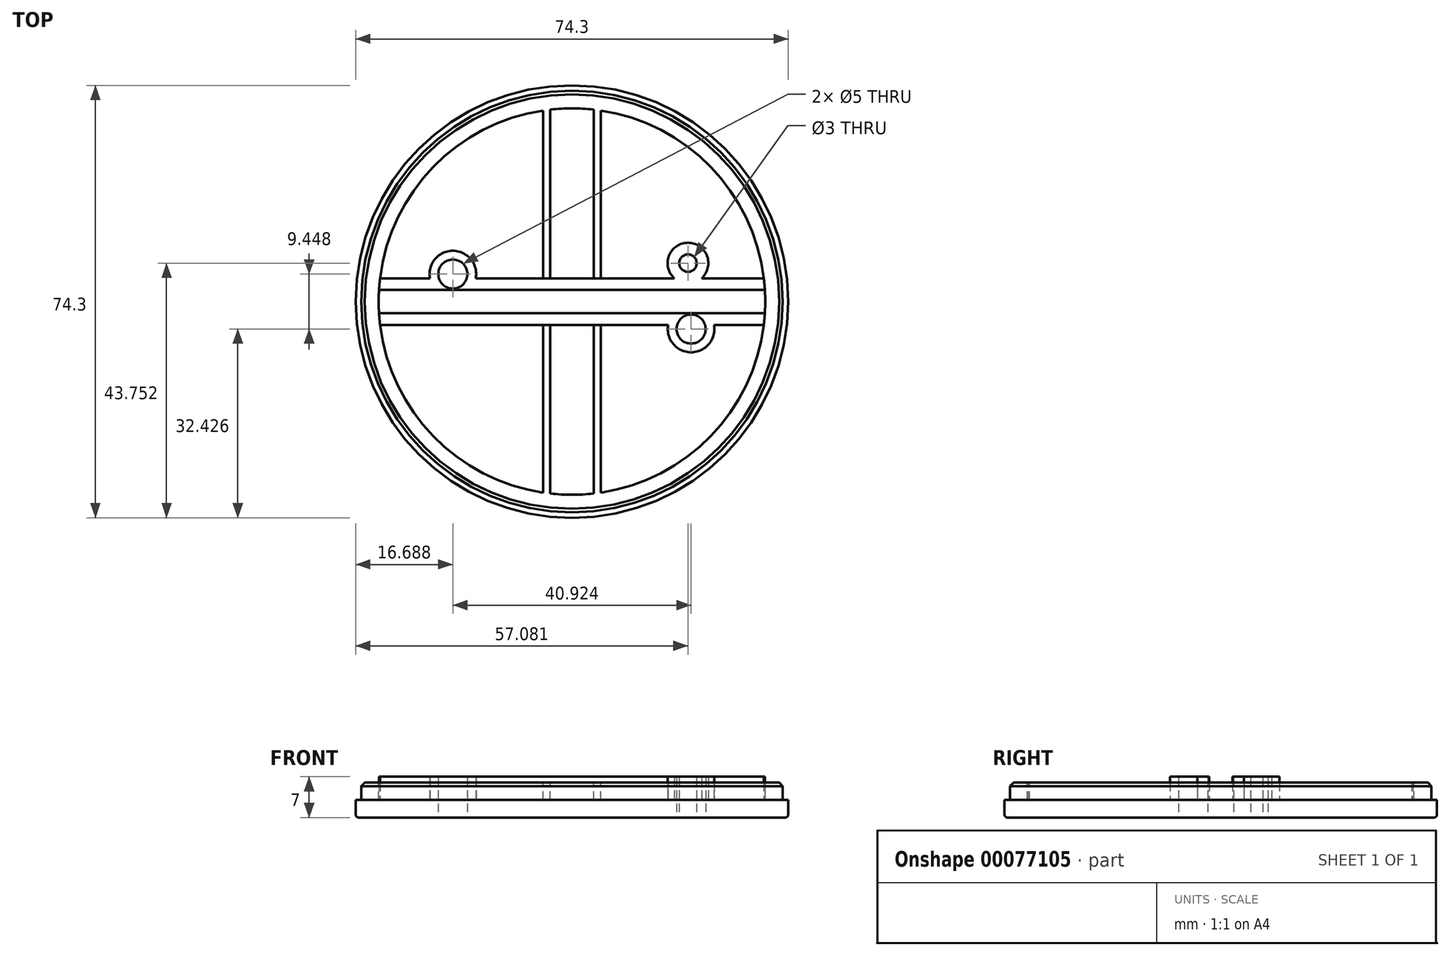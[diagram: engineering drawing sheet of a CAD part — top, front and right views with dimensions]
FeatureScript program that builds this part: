
annotation { "Feature Type Name" : "Feature", "Feature Type Description" : "" }
export const myFeature = defineFeature(function(context is Context, id is Id, definition is map)
    precondition{}
    {
        {
            var Q0;
            Q0=qCreatedBy(makeId("Front.planeOp"),FACE);
            var sketch = newSketch(context, id + "F0", { "sketchPlane" : qUnion([Q0])});
            skLineSegment(sketch, "E0.bottom", {"start": v(0, 0) * mm, "end": v(-33.2, 0) * mm});
            skLineSegment(sketch, "E0.top", {"start": v(0, -3) * mm, "end": v(-37.15, -3) * mm});
            skLineSegment(sketch, "E0.left", {"start": v(0, 0) * mm, "end": v(0, -3) * mm});
            skLineSegment(sketch, "E0.right", {"start": v(-37.15, 0) * mm, "end": v(-37.15, -3) * mm});
            skLineSegment(sketch, "E1.top", {"start": v(-36.2, 3) * mm, "end": v(-33.2, 3) * mm});
            skLineSegment(sketch, "E1.left", {"start": v(-36.2, 0) * mm, "end": v(-36.2, 3) * mm});
            skLineSegment(sketch, "E1.right", {"start": v(-33.2, 0) * mm, "end": v(-33.2, 3) * mm});
            skLineSegment(sketch, "E2.trimOffspring", {"start": v(-36.2, 0) * mm, "end": v(-37.15, 0) * mm});
            skLineSegment(sketch, "E3", {"start": v(0, 23.02) * mm, "end": v(0, -39) * mm, "construction": true});
            skSolve(sketch);
        }
        {
            var Q0;
            Q0=makeQuery(id+"F0.imprint","IMPRINT",FACE,{"disambiguationData":[TD([[makeQuery(id+"F0.imprint","IMPRINT",EDGE,{"derivedFrom":sQuery(id+"F0.wireOp",EDGE,"E0.bottom")}),1.0]])]});
            var Q1;
            Q1=sQuery(id+"F0.wireOp",EDGE,"E3");
            revolve(context, id + "F1", {"surfaceOperationType" : NewSurfaceOperationType.NEW, "entities" : qUnion([Q0]), "axis" : qUnion([Q1]), "revolveType" : RevolveType.FULL});
        }
        {
            var Q0;
            Q0=makeQuery(id+"F1.opRevolve","SWEPT_FACE",FACE,{"disambiguationData":[OSD([sQuery(id+"F0.wireOp",EDGE,"E0.bottom")])]});
            var sketch = newSketch(context, id + "F2", { "sketchPlane" : qUnion([Q0])});
            skLineSegment(sketch, "E4.bottom", {"start": v(-34.3, 2) * mm, "end": v(34, 2) * mm});
            skLineSegment(sketch, "E4.top", {"start": v(-34.3, 4) * mm, "end": v(34, 4) * mm});
            skLineSegment(sketch, "E4.left", {"start": v(-34.3, 2) * mm, "end": v(-34.3, 4) * mm});
            skLineSegment(sketch, "E4.right", {"start": v(34, 2) * mm, "end": v(34, 4) * mm});
            skLineSegment(sketch, "E5.MirrorCS", {"start": v(-34.3, -2) * mm, "end": v(34, -2) * mm});
            skLineSegment(sketch, "E6.MirrorCS", {"start": v(-34.3, -2) * mm, "end": v(-34.3, -4) * mm});
            skLineSegment(sketch, "E7.MirrorCS", {"start": v(-34.3, -4) * mm, "end": v(34, -4) * mm});
            skLineSegment(sketch, "E8.MirrorCS", {"start": v(34, -2) * mm, "end": v(34, -4) * mm});
            skSolve(sketch);
        }
        {
            var Q0;
            {var subQ0=sQuery(id+"F2.wireOp",EDGE,"E4.bottom");var subQ1=makeQuery(id+"F1.opRevolve","SWEPT_EDGE",EDGE,{"disambiguationData":[OSD([sQuery(id+"F0.wireOp",EDGE,"E0.bottom"),sQuery(id+"F0.wireOp",EDGE,"E1.right")])]});var subQ2=makeQuery(id+"F2.imprint","INTERSECT",VERTEX,{"disambiguationData":[OD(0.0)],"derivedFrom":[subQ1,subQ0]});Q0=makeQuery(id+"F2.imprint","IMPRINT",FACE,{"disambiguationData":[TD([[makeQuery(id+"F2.imprint","IMPRINT",EDGE,{"disambiguationData":[TD([[subQ2,-1.0]])],"derivedFrom":subQ0}),1.0]])]});}
            var Q1;
            {var subQ0=sQuery(id+"F2.wireOp",EDGE,"E5.MirrorCS");var subQ1=makeQuery(id+"F1.opRevolve","SWEPT_EDGE",EDGE,{"disambiguationData":[OSD([sQuery(id+"F0.wireOp",EDGE,"E0.bottom"),sQuery(id+"F0.wireOp",EDGE,"E1.right")])]});var subQ2=makeQuery(id+"F2.imprint","INTERSECT",VERTEX,{"disambiguationData":[OD(0.0)],"derivedFrom":[subQ1,subQ0]});Q1=makeQuery(id+"F2.imprint","IMPRINT",FACE,{"disambiguationData":[TD([[makeQuery(id+"F2.imprint","IMPRINT",EDGE,{"disambiguationData":[TD([[subQ2,-1.0]])],"derivedFrom":subQ0}),-1.0]])]});}
            extrude(context, id + "F3", {"entities" : qUnion([Q0, Q1]), "operationType" : NewBodyOperationType.ADD, "depth" : 4 * mm, "offsetDistance" : 25 * mm});
        }
        {
            var Q0;
            Q0=makeQuery(id+"F3.boolean.opBoolean","SPLIT",FACE,{"disambiguationData":[TD([makeQuery(id+"F3.opExtrude","SWEPT_FACE",FACE,{"disambiguationData":[OSD([sQuery(id+"F2.wireOp",EDGE,"E4.top")])]})])],"derivedFrom":makeQuery(id+"F1.opRevolve","SWEPT_FACE",FACE,{"disambiguationData":[OSD([sQuery(id+"F0.wireOp",EDGE,"E0.bottom")])]})});
            var sketch = newSketch(context, id + "F4", { "sketchPlane" : qUnion([Q0])});
            skCircle(sketch, "E9", {"center": v(0, 0) * mm, "radius": 25 * mm});
            skSolve(sketch);
        }
        {
            var Q0;
            {var subQ0=sQuery(id+"F4.wireOp",EDGE,"E9");var subQ1=sQuery(id+"F2.wireOp",EDGE,"E4.top");var subQ2=makeQuery(id+"F3.opExtrude","CAP_EDGE",EDGE,{"disambiguationData":[OSD([subQ1])],"isStart":true});var subQ3=makeQuery(id+"F4.imprint","INTERSECT",VERTEX,{"disambiguationData":[OD(0.0)],"derivedFrom":[subQ2,subQ0]});Q0=makeQuery(id+"F4.imprint","IMPRINT",FACE,{"disambiguationData":[TD([[makeQuery(id+"F4.imprint","IMPRINT",EDGE,{"disambiguationData":[TD([[subQ3,1.0]])],"derivedFrom":subQ0}),-1.0]])]});}
            var sketch = newSketch(context, id + "F5", { "sketchPlane" : qUnion([Q0])});
            skLineSegment(sketch, "E10", {"start": v(-33.33, 7.7) * mm, "end": v(0, 0) * mm, "construction": true});
            skLineSegment(sketch, "E11", {"start": v(0, 0) * mm, "end": v(33.42, -7.72) * mm, "construction": true});
            skLineSegment(sketch, "E12.bottom", {"start": v(-4.93, 3.16) * mm, "end": v(-3.73, 3.16) * mm});
            skLineSegment(sketch, "E12.top", {"start": v(-4.93, 33.8) * mm, "end": v(-3.73, 33.8) * mm});
            skLineSegment(sketch, "E12.left", {"start": v(-4.93, 3.16) * mm, "end": v(-4.93, 33.8) * mm});
            skLineSegment(sketch, "E12.right", {"start": v(-3.73, 3.16) * mm, "end": v(-3.73, 33.8) * mm});
            skLineSegment(sketch, "E13.MirrorCS", {"start": v(3.73, 3.16) * mm, "end": v(3.73, 33.8) * mm});
            skLineSegment(sketch, "E14.MirrorCS", {"start": v(4.93, 3.16) * mm, "end": v(4.93, 33.8) * mm});
            skLineSegment(sketch, "E15.MirrorCS", {"start": v(4.93, 33.8) * mm, "end": v(3.73, 33.8) * mm});
            skLineSegment(sketch, "E16.MirrorCS", {"start": v(4.93, 3.16) * mm, "end": v(3.73, 3.16) * mm});
            skLineSegment(sketch, "E17.MirrorCS", {"start": v(-4.93, -33.8) * mm, "end": v(-3.73, -33.8) * mm});
            skLineSegment(sketch, "E18.MirrorCS", {"start": v(-3.73, -3.16) * mm, "end": v(-3.73, -33.8) * mm});
            skLineSegment(sketch, "E19.MirrorCS", {"start": v(-4.93, -3.16) * mm, "end": v(-3.73, -3.16) * mm});
            skLineSegment(sketch, "E20.MirrorCS", {"start": v(-4.93, -3.16) * mm, "end": v(-4.93, -33.8) * mm});
            skLineSegment(sketch, "E21.MirrorCS", {"start": v(4.93, -3.16) * mm, "end": v(3.73, -3.16) * mm});
            skLineSegment(sketch, "E22.MirrorCS", {"start": v(4.93, -33.8) * mm, "end": v(3.73, -33.8) * mm});
            skLineSegment(sketch, "E23.MirrorCS", {"start": v(3.73, -3.16) * mm, "end": v(3.73, -33.8) * mm});
            skLineSegment(sketch, "E24.MirrorCS", {"start": v(4.93, -3.16) * mm, "end": v(4.93, -33.8) * mm});
            skCircle(sketch, "E25", {"center": v(0, 0) * mm, "radius": 21 * mm, "construction": true});
            skCircle(sketch, "E26", {"center": v(-20.46, 4.72) * mm, "radius": 2.5 * mm});
            skCircle(sketch, "E27", {"center": v(20.46, -4.72) * mm, "radius": 2.5 * mm});
            skArc(sketch, "E28", {"start": v(-17.49, 2.05) * mm, "mid": v(-20.46, 8.72) * mm, "end": v(-23.44, 2.05) * mm});
            skArc(sketch, "E29", {"start": v(17.54, -2) * mm, "mid": v(20.46, -8.72) * mm, "end": v(23.38, -2) * mm});
            skLineSegment(sketch, "E30", {"start": v(-23.44, 2.05) * mm, "end": v(-17.49, 2.05) * mm});
            skLineSegment(sketch, "E31", {"start": v(17.54, -2) * mm, "end": v(23.38, -2) * mm});
            skSolve(sketch);
        }
        {
            var Q0;
            Q0=makeQuery(id+"F5.imprint","IMPRINT",FACE,{"disambiguationData":[TD([[makeQuery(id+"F5.imprint","IMPRINT",EDGE,{"derivedFrom":sQuery(id+"F5.wireOp",EDGE,"E17.MirrorCS")}),1.0]])]});
            var Q1;
            Q1=makeQuery(id+"F5.imprint","IMPRINT",FACE,{"disambiguationData":[TD([[makeQuery(id+"F5.imprint","IMPRINT",EDGE,{"derivedFrom":sQuery(id+"F5.wireOp",EDGE,"E21.MirrorCS")}),1.0]])]});
            var Q2;
            {var subQ0=sQuery(id+"F5.wireOp",EDGE,"E12.bottom");Q2=makeQuery(id+"F5.imprint","IMPRINT",FACE,{"disambiguationData":[TD([[makeQuery(id+"F5.imprint","IMPRINT",EDGE,{"derivedFrom":subQ0}),1.0]])]});}
            var Q3;
            {var subQ0=sQuery(id+"F5.wireOp",EDGE,"E16.MirrorCS");Q3=makeQuery(id+"F5.imprint","IMPRINT",FACE,{"disambiguationData":[TD([[makeQuery(id+"F5.imprint","IMPRINT",EDGE,{"derivedFrom":subQ0}),-1.0]])]});}
            var Q4;
            {var subQ0=sQuery(id+"F5.wireOp",EDGE,"E13.MirrorCS");var subQ1=sQuery(id+"F4.wireOp",EDGE,"E9");var subQ2=sQuery(id+"F2.wireOp",EDGE,"E4.top");var subQ3=makeQuery(id+"F3.opExtrude","CAP_EDGE",EDGE,{"disambiguationData":[OSD([subQ2])],"isStart":true});var subQ4=makeQuery(id+"F4.imprint","IMPRINT",EDGE,{"disambiguationData":[TD([[makeQuery(id+"F4.imprint","INTERSECT",VERTEX,{"disambiguationData":[OD(0.0)],"derivedFrom":[subQ3,subQ1]}),1.0]])],"derivedFrom":subQ1});var subQ5=makeQuery(id+"F5.imprint","INTERSECT",VERTEX,{"derivedFrom":[subQ4,subQ0]});Q4=makeQuery(id+"F5.imprint","IMPRINT",FACE,{"disambiguationData":[TD([[makeQuery(id+"F5.imprint","IMPRINT",EDGE,{"disambiguationData":[TD([[subQ5,-1.0]])],"derivedFrom":subQ0}),-1.0]])]});}
            var Q5;
            {var subQ0=sQuery(id+"F5.wireOp",EDGE,"E12.left");var subQ1=sQuery(id+"F4.wireOp",EDGE,"E9");var subQ2=sQuery(id+"F2.wireOp",EDGE,"E4.top");var subQ3=makeQuery(id+"F3.opExtrude","CAP_EDGE",EDGE,{"disambiguationData":[OSD([subQ2])],"isStart":true});var subQ4=makeQuery(id+"F4.imprint","IMPRINT",EDGE,{"disambiguationData":[TD([[makeQuery(id+"F4.imprint","INTERSECT",VERTEX,{"disambiguationData":[OD(0.0)],"derivedFrom":[subQ3,subQ1]}),1.0]])],"derivedFrom":subQ1});var subQ5=makeQuery(id+"F5.imprint","INTERSECT",VERTEX,{"derivedFrom":[subQ4,subQ0]});Q5=makeQuery(id+"F5.imprint","IMPRINT",FACE,{"disambiguationData":[TD([[makeQuery(id+"F5.imprint","IMPRINT",EDGE,{"disambiguationData":[TD([[subQ5,-1.0]])],"derivedFrom":subQ0}),-1.0]])]});}
            extrude(context, id + "F6", {"entities" : qUnion([Q0, Q1, Q2, Q3, Q4, Q5]), "operationType" : NewBodyOperationType.ADD, "depth" : 3 * mm, "offsetDistance" : 25 * mm});
        }
        {
            var Q0;
            Q0=makeQuery(id+"F5.imprint","IMPRINT",FACE,{"disambiguationData":[TD([[makeQuery(id+"F5.imprint","IMPRINT",EDGE,{"derivedFrom":sQuery(id+"F5.wireOp",EDGE,"E27")}),-1.0]])]});
            var Q1;
            Q1=makeQuery(id+"F5.imprint","IMPRINT",FACE,{"disambiguationData":[TD([[makeQuery(id+"F5.imprint","IMPRINT",EDGE,{"derivedFrom":sQuery(id+"F5.wireOp",EDGE,"E26")}),-1.0]])]});
            extrude(context, id + "F7", {"entities" : qUnion([Q0, Q1]), "operationType" : NewBodyOperationType.ADD, "depth" : 4 * mm, "offsetDistance" : 25 * mm});
        }
        {
            var Q0;
            {var subQ0=sQuery(id+"F5.wireOp",EDGE,"E26");var subQ1=sQuery(id+"F4.wireOp",EDGE,"E9");var subQ2=makeQuery(id+"F3.opExtrude","CAP_EDGE",EDGE,{"disambiguationData":[OSD([sQuery(id+"F2.wireOp",EDGE,"E4.top")])],"isStart":true});var subQ3=makeQuery(id+"F4.imprint","IMPRINT",EDGE,{"disambiguationData":[TD([[makeQuery(id+"F4.imprint","INTERSECT",VERTEX,{"disambiguationData":[OD(0.0)],"derivedFrom":[subQ2,subQ1]}),1.0]])],"derivedFrom":subQ1});var subQ4=makeQuery(id+"F5.imprint","INTERSECT",VERTEX,{"disambiguationData":[OD(0.0)],"derivedFrom":[subQ3,subQ0]});Q0=makeQuery(id+"F5.imprint","IMPRINT",FACE,{"disambiguationData":[TD([[makeQuery(id+"F5.imprint","IMPRINT",EDGE,{"disambiguationData":[TD([[subQ4,-1.0]])],"derivedFrom":subQ0}),1.0]])]});}
            var Q1;
            {var subQ0=sQuery(id+"F5.wireOp",EDGE,"E26");var subQ1=sQuery(id+"F4.wireOp",EDGE,"E9");var subQ2=makeQuery(id+"F3.opExtrude","CAP_EDGE",EDGE,{"disambiguationData":[OSD([sQuery(id+"F2.wireOp",EDGE,"E4.top")])],"isStart":true});var subQ3=makeQuery(id+"F4.imprint","IMPRINT",EDGE,{"disambiguationData":[TD([[makeQuery(id+"F4.imprint","INTERSECT",VERTEX,{"disambiguationData":[OD(0.0)],"derivedFrom":[subQ2,subQ1]}),1.0]])],"derivedFrom":subQ1});var subQ4=makeQuery(id+"F5.imprint","INTERSECT",VERTEX,{"disambiguationData":[OD(0.0)],"derivedFrom":[subQ3,subQ0]});Q1=makeQuery(id+"F5.imprint","IMPRINT",FACE,{"disambiguationData":[TD([[makeQuery(id+"F5.imprint","IMPRINT",EDGE,{"disambiguationData":[TD([[subQ4,1.0]])],"derivedFrom":subQ0}),1.0]])]});}
            var Q2;
            Q2=makeQuery(id+"F5.imprint","IMPRINT",FACE,{"disambiguationData":[TD([[makeQuery(id+"F5.imprint","IMPRINT",EDGE,{"derivedFrom":sQuery(id+"F5.wireOp",EDGE,"E27")}),1.0]])]});
            extrude(context, id + "F8", {"entities" : qUnion([Q0, Q1, Q2]), "operationType" : NewBodyOperationType.REMOVE, "oppositeDirection" : true, "depth" : 25 * mm, "offsetDistance" : 25 * mm, "symmetric" : true});
        }
        {
            var Q0;
            {var subQ0=sQuery(id+"F4.wireOp",EDGE,"E9");var subQ1=makeQuery(id+"F3.opExtrude","CAP_EDGE",EDGE,{"disambiguationData":[OSD([sQuery(id+"F2.wireOp",EDGE,"E4.top")])],"isStart":true});var subQ2=makeQuery(id+"F4.imprint","INTERSECT",VERTEX,{"disambiguationData":[OD(0.0)],"derivedFrom":[subQ1,subQ0]});Q0=makeQuery(id+"F4.imprint","IMPRINT",FACE,{"disambiguationData":[TD([[makeQuery(id+"F4.imprint","IMPRINT",EDGE,{"disambiguationData":[TD([[subQ2,1.0]])],"derivedFrom":subQ0}),1.0]])]});}
            var sketch = newSketch(context, id + "F9", { "sketchPlane" : qUnion([Q0])});
            skCircle(sketch, "E32", {"center": v(19.93, 6.6) * mm, "radius": 1.5 * mm});
            skCircle(sketch, "E33", {"center": v(19.93, 6.6) * mm, "radius": 3.5 * mm});
            skSolve(sketch);
        }
        {
            var Q0;
            Q0=makeQuery(id+"F1.opRevolve","SWEPT_EDGE",EDGE,{"disambiguationData":[OSD([sQuery(id+"F0.wireOp",EDGE,"E1.top"),sQuery(id+"F0.wireOp",EDGE,"E1.left")])]});
            chamfer(context, id + "F10", {"entities" : qUnion([Q0]), "width" : .6 * mm, "tangentPropagation" : true});
        }
        {
            var Q0;
            Q0=makeQuery(id+"F1.opRevolve","SWEPT_EDGE",EDGE,{"disambiguationData":[OSD([sQuery(id+"F0.wireOp",EDGE,"E0.top"),sQuery(id+"F0.wireOp",EDGE,"E0.right")])]});
            fillet(context, id + "F11", {"entities" : qUnion([Q0]), "radius" : .5 * mm, "tangentPropagation" : true, "allowEdgeOverflow" : false});
        }
        {
            var Q0;
            Q0=makeQuery(id+"F9.imprint","IMPRINT",FACE,{"disambiguationData":[TD([[makeQuery(id+"F9.imprint","IMPRINT",EDGE,{"derivedFrom":sQuery(id+"F9.wireOp",EDGE,"E32")}),-1.0]])]});
            extrude(context, id + "F12", {"entities" : qUnion([Q0]), "operationType" : NewBodyOperationType.ADD, "depth" : 4 * mm, "offsetDistance" : 25 * mm});
        }
        {
            var Q0;
            Q0=makeQuery(id+"F9.imprint","IMPRINT",FACE,{"disambiguationData":[TD([[makeQuery(id+"F9.imprint","IMPRINT",EDGE,{"derivedFrom":sQuery(id+"F9.wireOp",EDGE,"E32")}),1.0]])]});
            extrude(context, id + "F13", {"entities" : qUnion([Q0]), "operationType" : NewBodyOperationType.REMOVE, "oppositeDirection" : true, "depth" : 25 * mm, "offsetDistance" : 25 * mm});
        }
    });
